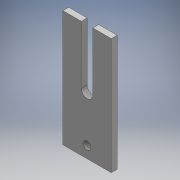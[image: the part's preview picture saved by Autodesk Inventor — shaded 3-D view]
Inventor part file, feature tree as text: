
AUTODESK INVENTOR PART (.ipt)
format: ipt  version: 2016 (Build 200138000, 138)  size: 105,984 bytes
history: native  units: mm
features: sketch x4, extrude x2, hole x2
ambient origin geometry x8: Origin, YZ Plane, XZ Plane, XY Plane, X Axis, Y Axis, Z Axis, Center Point
bodies: Solid1 (feature_tree)
feature tree (8):
  extrude  "Extrusion1"  Depth=60.0mm
  hole  "Hole2"  [1 undecoded]
  hole  "Hole3"  [1 undecoded]
  extrude  "Extrusion2"  [1 undecoded]
  sketch  "Sketch1"  dims[d0=25.0mm d1=60.0mm]
  sketch  "Sketch2"  dims[d2=3.0mm d3=0.0mm d15=6.0mm]
  sketch  "Sketch3"  dims[d16=4.0mm d17=6.0mm d18=4.0mm d19=2.0mm d20=90.0deg d21=8.0mm d22=20.594885mm]
  sketch  "Sketch4"  dims[d23=6.0mm d24=6.0mm d25=4.0mm d26=2.0mm d27=90.0deg d28=8.0mm d29=20.594885mm d30=3.0mm d31=0.0mm]
note: 3 required parameter values undecoded (feature->parameter linkage not recoverable at this tier; creation-order binding heuristic only, values carry confidence <= 0.55)
